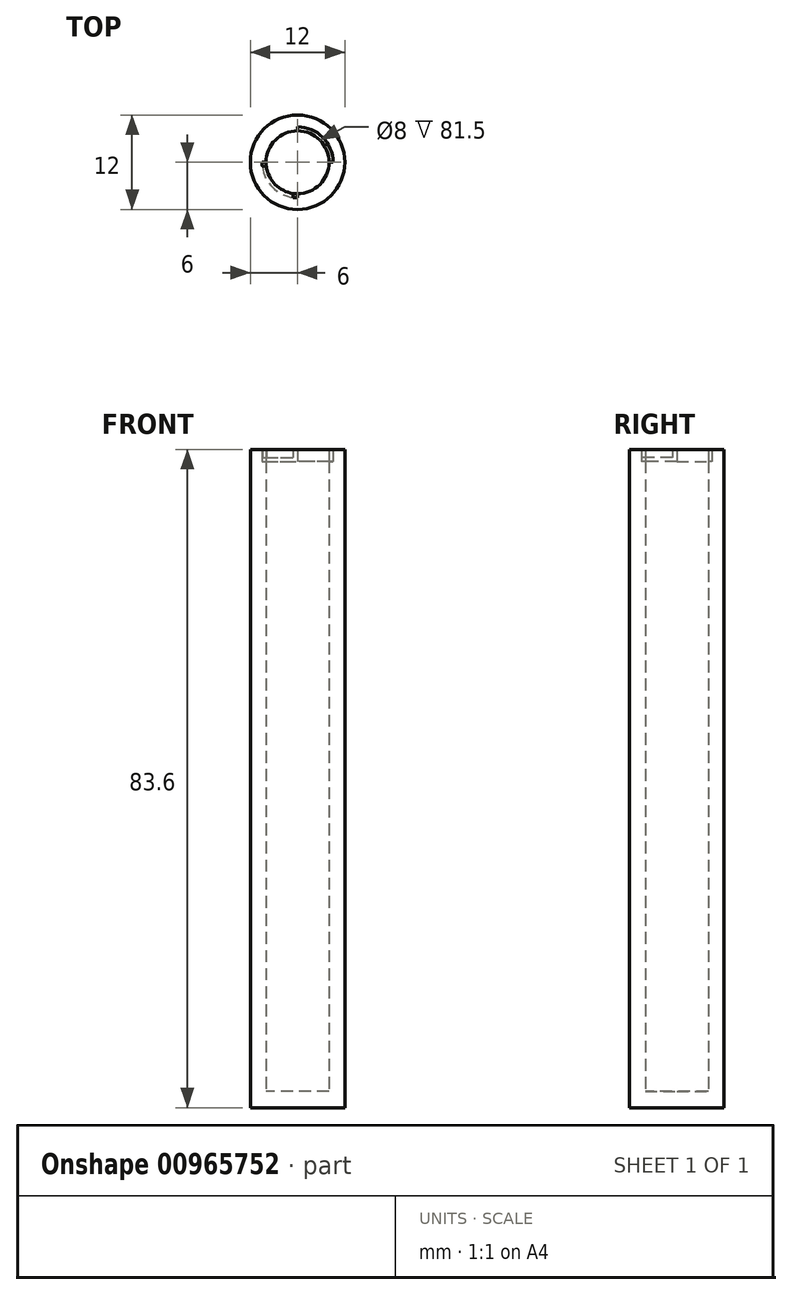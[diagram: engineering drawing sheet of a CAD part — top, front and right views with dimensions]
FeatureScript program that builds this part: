
annotation { "Feature Type Name" : "Feature", "Feature Type Description" : "" }
export const myFeature = defineFeature(function(context is Context, id is Id, definition is map)
    precondition{}
    {
        {
            var Q0;
            Q0=qCreatedBy(makeId("Top.planeOp"),FACE);
            var sketch = newSketch(context, id + "F0", { "sketchPlane" : qUnion([Q0])});
            skCircle(sketch, "E0", {"center": v(0, 0) * mm, "radius": 6 * mm});
            skSolve(sketch);
        }
        {
            var Q0;
            Q0 = qSketchRegion(id + "F0", true);
            extrude(context, id + "F1", {"entities" : qUnion([Q0]), "depth" : 2.1 * mm, "offsetDistance" : 25 * mm});
        }
        {
            var Q0;
            Q0=makeQuery(id+"F1.opExtrude","CAP_FACE",FACE,{"disambiguationData":[OSD([sQuery(id+"F0.wireOp",EDGE,"E0")])],"isStart":false});
            var sketch = newSketch(context, id + "F2", { "sketchPlane" : qUnion([Q0])});
            skCircle(sketch, "E1", {"center": v(0, 0) * mm, "radius": 4 * mm});
            skCircle(sketch, "E2", {"center": v(0, 0) * mm, "radius": 6 * mm});
            skSolve(sketch);
        }
        {
            var Q0;
            Q0 = qSketchRegion(id + "F2", true);
            extrude(context, id + "F3", {"entities" : qUnion([Q0]), "operationType" : NewBodyOperationType.ADD, "depth" : 80 * mm, "offsetDistance" : 25 * mm});
        }
        {
            var Q0;
            Q0=makeQuery(id+"F3.opExtrude","CAP_FACE",FACE,{"disambiguationData":[OSD([sQuery(id+"F2.wireOp",EDGE,"E1"),sQuery(id+"F2.wireOp",EDGE,"E2")])],"isStart":false});
            var sketch = newSketch(context, id + "F4", { "sketchPlane" : qUnion([Q0])});
            skCircle(sketch, "E3.0", {"center": v(0, 0) * mm, "radius": 6 * mm});
            skArc(sketch, "E4", {"start": v(0, 4.5) * mm, "mid": v(3.18, 3.18) * mm, "end": v(4.5, 0) * mm});
            skArc(sketch, "E5", {"start": v(0, -4.5) * mm, "mid": v(-3.18, -3.18) * mm, "end": v(-4.5, 0) * mm});
            skArc(sketch, "E6", {"start": v(0, 4) * mm, "mid": v(-2.83, 2.83) * mm, "end": v(-4, 0) * mm});
            skArc(sketch, "E7", {"start": v(4, 0) * mm, "mid": v(2.83, -2.83) * mm, "end": v(0, -4) * mm});
            skLineSegment(sketch, "E8", {"start": v(-4.5, 0) * mm, "end": v(-4, 0) * mm});
            skLineSegment(sketch, "E9", {"start": v(0, 4.5) * mm, "end": v(0, 4) * mm});
            skLineSegment(sketch, "E10", {"start": v(4, 0) * mm, "end": v(4.5, 0) * mm});
            skLineSegment(sketch, "E11", {"start": v(0, -4) * mm, "end": v(0, -4.5) * mm});
            skSolve(sketch);
        }
        {
            var Q0;
            Q0 = qSketchRegion(id + "F4", true);
            extrude(context, id + "F5", {"entities" : qUnion([Q0]), "operationType" : NewBodyOperationType.ADD, "depth" : .5 * mm, "offsetDistance" : 25 * mm});
        }
        {
            var Q0;
            Q0=makeQuery(id+"F5.opExtrude","CAP_FACE",FACE,{"disambiguationData":[OSD([sQuery(id+"F4.wireOp",EDGE,"E3.0"),sQuery(id+"F4.wireOp",EDGE,"E4"),sQuery(id+"F4.wireOp",EDGE,"E5"),sQuery(id+"F4.wireOp",EDGE,"E6"),sQuery(id+"F4.wireOp",EDGE,"E7"),sQuery(id+"F4.wireOp",EDGE,"E8"),sQuery(id+"F4.wireOp",EDGE,"E9"),sQuery(id+"F4.wireOp",EDGE,"E10"),sQuery(id+"F4.wireOp",EDGE,"E11")])],"isStart":false});
            var sketch = newSketch(context, id + "F6", { "sketchPlane" : qUnion([Q0])});
            skArc(sketch, "E12.0", {"start": v(0, 4) * mm, "mid": v(-2.83, 2.83) * mm, "end": v(-4, 0) * mm});
            skLineSegment(sketch, "E13.0", {"start": v(-4.5, 0) * mm, "end": v(-4, 0) * mm});
            skArc(sketch, "E14.0", {"start": v(0, -4) * mm, "mid": v(2.83, -2.83) * mm, "end": v(4, 0) * mm});
            skLineSegment(sketch, "E15.0", {"start": v(0, 4.5) * mm, "end": v(0, 4) * mm});
            skLineSegment(sketch, "E16.0", {"start": v(4, 0) * mm, "end": v(4.5, 0) * mm});
            skLineSegment(sketch, "E17.0", {"start": v(0, -4) * mm, "end": v(0, -4.5) * mm});
            skLineSegment(sketch, "E18", {"start": v(0, -4.5) * mm, "end": v(0, -4.5) * mm});
            skArc(sketch, "E19", {"start": v(0, -4) * mm, "mid": v(-2.64, -3) * mm, "end": v(-3.97, -0.5) * mm});
            skArc(sketch, "E20", {"start": v(-4.47, -0.55) * mm, "mid": v(-4.5, -0.28) * mm, "end": v(-4.5, 0) * mm});
            skLineSegment(sketch, "E21", {"start": v(-4.47, -0.55) * mm, "end": v(-3.97, -0.5) * mm});
            skArc(sketch, "E22", {"start": v(0, -4.5) * mm, "mid": v(-0.28, -4.5) * mm, "end": v(-0.55, -4.47) * mm});
            skArc(sketch, "E23", {"start": v(-3.97, -0.5) * mm, "mid": v(2.84, 2.81) * mm, "end": v(-0.55, -3.96) * mm});
            skLineSegment(sketch, "E24", {"start": v(-0.55, -3.96) * mm, "end": v(-0.55, -4.47) * mm});
            skSolve(sketch);
        }
        {
            var Q0;
            {var subQ3=sQuery(id+"F6.wireOp",EDGE,"E21");Q0=makeQuery(id+"F6.imprint","IMPRINT",FACE,{"disambiguationData":[TD([[makeQuery(id+"F6.imprint","IMPRINT",EDGE,{"derivedFrom":subQ3}),-1.0]])]});}
            var Q1;
            {var subQ2=sQuery(id+"F6.wireOp",EDGE,"E13.0");Q1=makeQuery(id+"F6.imprint","IMPRINT",FACE,{"disambiguationData":[TD([[makeQuery(id+"F6.imprint","IMPRINT",EDGE,{"derivedFrom":subQ2}),1.0]])]});}
            extrude(context, id + "F7", {"entities" : qUnion([Q0, Q1]), "operationType" : NewBodyOperationType.ADD, "depth" : 1 * mm, "offsetDistance" : 25 * mm});
        }
    });
